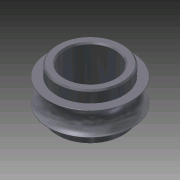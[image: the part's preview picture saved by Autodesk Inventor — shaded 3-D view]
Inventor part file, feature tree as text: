
AUTODESK INVENTOR PART (.ipt)
format: ipt  version: 2011 (Build 150239000, 239)  size: 162,816 bytes
history: native  units: in
note: dims shown in document units (in); Inventor stores cm internally (conversion verified against a paired STEP export)
features: chamfer x2, revolve x1, sketch x1
ambient origin geometry x8: Origin, YZ Plane, XZ Plane, XY Plane, X Axis, Y Axis, Z Axis, Center Point
bodies: Solid1 (feature_tree)
feature tree (4):
  revolve  "Revolution1"  [1 undecoded]
  chamfer  "Chamfer1"  Distance=0.0625in
  chamfer  "Chamfer2"  Distance=0.18in
  sketch  "Sketch1"  dims[d0=0.0856in d2=0.0856in d3=0.0625in d7=0.18in d8=0.003in d9=90.0deg d10=0.01in d11=0.125in d12=45.0deg d13=0.01in d14=0.125in d15=45.0deg d16=0.1875in d20=0.1236in d21=0.1565in]
note: 1 required parameter value undecoded (feature->parameter linkage not recoverable at this tier; creation-order binding heuristic only, values carry confidence <= 0.55)
